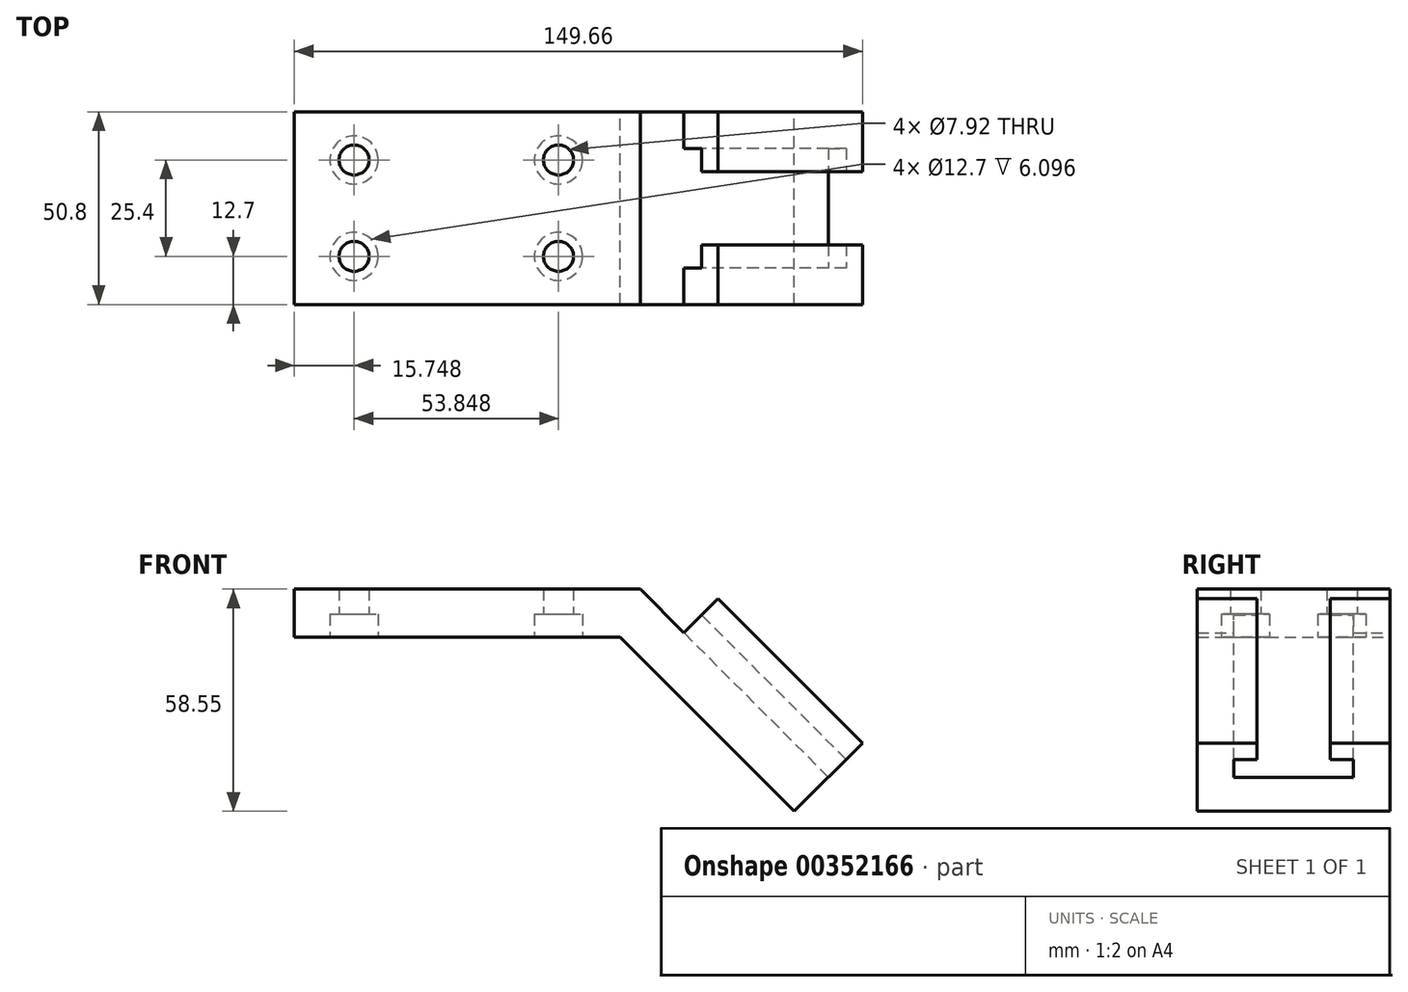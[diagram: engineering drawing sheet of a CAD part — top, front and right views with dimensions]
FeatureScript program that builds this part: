
annotation { "Feature Type Name" : "Feature", "Feature Type Description" : "" }
export const myFeature = defineFeature(function(context is Context, id is Id, definition is map)
    precondition{}
    {
        {
            var Q0;
            Q0=qCreatedBy(makeId("Front.planeOp"),FACE);
            var sketch = newSketch(context, id + "F0", { "sketchPlane" : qUnion([Q0])});
            skLineSegment(sketch, "E0", {"start": v(0, 0) * mm, "end": v(0, 12.7) * mm});
            skLineSegment(sketch, "E1", {"start": v(0, 12.7) * mm, "end": v(91.11, 12.7) * mm});
            skLineSegment(sketch, "E2", {"start": v(0, 0) * mm, "end": v(85.85, 0) * mm});
            skLineSegment(sketch, "E3", {"start": v(85.85, 0) * mm, "end": v(131.7, -45.85) * mm});
            skLineSegment(sketch, "E4", {"start": v(111.59, 10.19) * mm, "end": v(149.66, -27.9) * mm});
            skLineSegment(sketch, "E5", {"start": v(149.66, -27.9) * mm, "end": v(131.7, -45.85) * mm});
            skLineSegment(sketch, "E6", {"start": v(91.11, 12.7) * mm, "end": v(102.6, 1.2) * mm});
            skLineSegment(sketch, "E7", {"start": v(102.6, 1.2) * mm, "end": v(111.59, 10.19) * mm});
            skSolve(sketch);
        }
        {
            var Q0;
            Q0=makeQuery(id+"F0.imprint","IMPRINT",FACE,{"disambiguationData":[TD([[makeQuery(id+"F0.imprint","IMPRINT",EDGE,{"derivedFrom":sQuery(id+"F0.wireOp",EDGE,"E0")}),-1.0]])]});
            extrude(context, id + "F1", {"entities" : qUnion([Q0]), "depth" : 50.8 * mm});
        }
        {
            var Q0;
            Q0=makeQuery(id+"F1.opExtrude","SWEPT_FACE",FACE,{"disambiguationData":[OSD([sQuery(id+"F0.wireOp",EDGE,"E4")])]});
            var sketch = newSketch(context, id + "F2", { "sketchPlane" : qUnion([Q0])});
            skLineSegment(sketch, "E8", {"start": v(125.55, 0) * mm, "end": v(125.55, -50.8) * mm});
            skLineSegment(sketch, "E9", {"start": v(125.55, -50.8) * mm, "end": v(119.18, -50.8) * mm});
            skLineSegment(sketch, "E10", {"start": v(125.55, 0) * mm, "end": v(119.18, 0) * mm});
            skArc(sketch, "E11", {"start": v(119.18, -50.8) * mm, "mid": v(125.55, -25.4) * mm, "end": v(119.18, 0) * mm});
            skSolve(sketch);
        }
        {
            var Q0;
            Q0 = qSketchRegion(id + "F2", true);
            extrude(context, id + "F3", {"entities" : qUnion([Q0]), "operationType" : NewBodyOperationType.REMOVE, "oppositeDirection" : true, "depth" : 25.4 * mm});
        }
        {
            var Q0;
            Q0=makeQuery(id+"F1.opExtrude","SWEPT_FACE",FACE,{"disambiguationData":[OSD([sQuery(id+"F0.wireOp",EDGE,"E7")])]});
            var sketch = newSketch(context, id + "F4", { "sketchPlane" : qUnion([Q0])});
            skLineSegment(sketch, "E12", {"start": v(35.05, 80.01) * mm, "end": v(35.05, 86.1) * mm});
            skLineSegment(sketch, "E13", {"start": v(35.05, 86.1) * mm, "end": v(15.75, 86.1) * mm});
            skLineSegment(sketch, "E14", {"start": v(15.75, 86.1) * mm, "end": v(15.75, 80.01) * mm});
            skLineSegment(sketch, "E15", {"start": v(15.75, 80.01) * mm, "end": v(9.65, 80.01) * mm});
            skLineSegment(sketch, "E16", {"start": v(9.65, 80.01) * mm, "end": v(9.65, 73.4) * mm});
            skLineSegment(sketch, "E17", {"start": v(9.65, 73.4) * mm, "end": v(41.15, 73.4) * mm});
            skLineSegment(sketch, "E18", {"start": v(41.15, 73.4) * mm, "end": v(41.15, 80.01) * mm});
            skLineSegment(sketch, "E19", {"start": v(41.15, 80.01) * mm, "end": v(35.05, 80.01) * mm});
            skSolve(sketch);
        }
        {
            var Q0;
            Q0=makeQuery(id+"F4.imprint","IMPRINT",FACE,{"disambiguationData":[TD([[makeQuery(id+"F4.imprint","IMPRINT",EDGE,{"derivedFrom":sQuery(id+"F4.wireOp",EDGE,"E12")}),1.0]])]});
            extrude(context, id + "F5", {"entities" : qUnion([Q0]), "operationType" : NewBodyOperationType.REMOVE, "endBound" : BoundingType.THROUGH_ALL, "oppositeDirection" : true, "depth" : 25.4 * mm});
        }
        {
            var Q0;
            Q0=makeQuery(id+"F1.opExtrude","SWEPT_FACE",FACE,{"disambiguationData":[OSD([sQuery(id+"F0.wireOp",EDGE,"E2")])]});
            var sketch = newSketch(context, id + "F6", { "sketchPlane" : qUnion([Q0])});
            skCircle(sketch, "E20", {"center": v(15.75, 12.7) * mm, "radius": 3.96 * mm});
            skCircle(sketch, "E21", {"center": v(15.75, 12.7) * mm, "radius": 6.35 * mm});
            skCircle(sketch, "E22.0.1.0", {"center": v(15.75, 38.1) * mm, "radius": 6.35 * mm});
            skCircle(sketch, "E22.0.1.1", {"center": v(15.75, 38.1) * mm, "radius": 3.96 * mm});
            skCircle(sketch, "E22.1.0.0", {"center": v(69.6, 12.7) * mm, "radius": 6.35 * mm});
            skCircle(sketch, "E22.1.0.1", {"center": v(69.6, 12.7) * mm, "radius": 3.96 * mm});
            skCircle(sketch, "E22.1.1.0", {"center": v(69.6, 38.1) * mm, "radius": 6.35 * mm});
            skCircle(sketch, "E22.1.1.1", {"center": v(69.6, 38.1) * mm, "radius": 3.96 * mm});
            skLineSegment(sketch, "E22.direction1", {"start": v(15.75, 12.7) * mm, "end": v(69.6, 12.7) * mm, "construction": true});
            skLineSegment(sketch, "E22.direction2", {"start": v(15.75, 12.7) * mm, "end": v(15.75, 38.1) * mm, "construction": true});
            skSolve(sketch);
        }
        {
            var Q0;
            Q0=makeQuery(id+"F6.imprint","IMPRINT",FACE,{"disambiguationData":[TD([[makeQuery(id+"F6.imprint","IMPRINT",EDGE,{"derivedFrom":sQuery(id+"F6.wireOp",EDGE,"E20")}),1.0]])]});
            var Q1;
            Q1=makeQuery(id+"F6.imprint","IMPRINT",FACE,{"disambiguationData":[TD([[makeQuery(id+"F6.imprint","IMPRINT",EDGE,{"derivedFrom":sQuery(id+"F6.wireOp",EDGE,"E22.0.1.1")}),1.0]])]});
            var Q2;
            Q2=makeQuery(id+"F6.imprint","IMPRINT",FACE,{"disambiguationData":[TD([[makeQuery(id+"F6.imprint","IMPRINT",EDGE,{"derivedFrom":sQuery(id+"F6.wireOp",EDGE,"E22.1.1.1")}),1.0]])]});
            var Q3;
            Q3=makeQuery(id+"F6.imprint","IMPRINT",FACE,{"disambiguationData":[TD([[makeQuery(id+"F6.imprint","IMPRINT",EDGE,{"derivedFrom":sQuery(id+"F6.wireOp",EDGE,"E22.1.0.1")}),1.0]])]});
            extrude(context, id + "F7", {"entities" : qUnion([Q0, Q1, Q2, Q3]), "operationType" : NewBodyOperationType.REMOVE, "endBound" : BoundingType.THROUGH_ALL, "oppositeDirection" : true, "depth" : 25.4 * mm});
        }
        {
            var Q0;
            Q0 = qSketchRegion(id + "F6", true);
            extrude(context, id + "F8", {"entities" : qUnion([Q0]), "operationType" : NewBodyOperationType.REMOVE, "oppositeDirection" : true, "depth" : 6.1 * mm});
        }
    });
